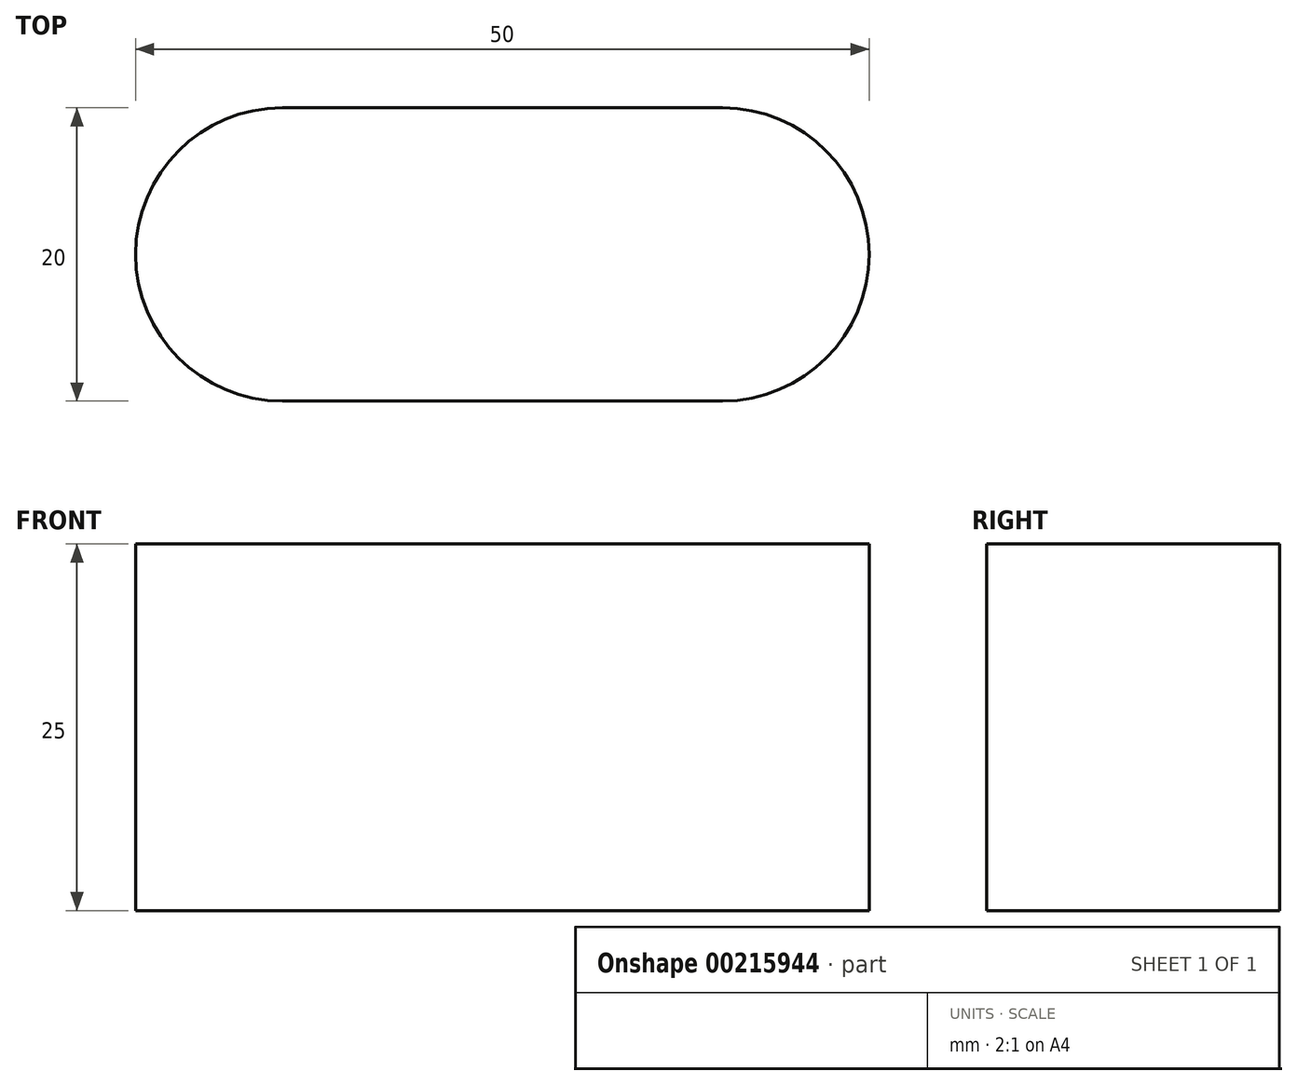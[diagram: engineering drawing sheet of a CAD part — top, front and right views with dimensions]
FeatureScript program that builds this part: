
annotation { "Feature Type Name" : "Feature", "Feature Type Description" : "" }
export const myFeature = defineFeature(function(context is Context, id is Id, definition is map)
    precondition{}
    {
        {
            var Q0;
            Q0=qCreatedBy(makeId("Top.planeOp"),FACE);
            var sketch = newSketch(context, id + "F0", { "sketchPlane" : qUnion([Q0])});
            skLineSegment(sketch, "E0.bottom", {"start": v(15, -10) * mm, "end": v(-15, -10) * mm});
            skLineSegment(sketch, "E0.top", {"start": v(15, 10) * mm, "end": v(-15, 10) * mm});
            skLineSegment(sketch, "E0.left", {"start": v(25, 0) * mm, "end": v(25, 0) * mm});
            skLineSegment(sketch, "E0.right", {"start": v(-25, 0) * mm, "end": v(-25, 0) * mm});
            skPoint(sketch, "E0.middle", {"position": v(0, 0) * mm});
            skPoint(sketch, "E1.visualSharp", {"position": v(-25, 10) * mm});
            skArc(sketch, "E1.filletArc", {"start": v(-15, 10) * mm, "mid": v(-22.07, 7.07) * mm, "end": v(-25, 0) * mm});
            skPoint(sketch, "E2.visualSharp", {"position": v(-25, -10) * mm});
            skArc(sketch, "E2.filletArc", {"start": v(-25, 0) * mm, "mid": v(-22.07, -7.07) * mm, "end": v(-15, -10) * mm});
            skPoint(sketch, "E3.visualSharp", {"position": v(25, -10) * mm});
            skArc(sketch, "E3.filletArc", {"start": v(15, -10) * mm, "mid": v(22.07, -7.07) * mm, "end": v(25, 0) * mm});
            skPoint(sketch, "E4.visualSharp", {"position": v(25, 10) * mm});
            skArc(sketch, "E4.filletArc", {"start": v(25, 0) * mm, "mid": v(22.07, 7.07) * mm, "end": v(15, 10) * mm});
            skSolve(sketch);
        }
        {
            var Q0;
            Q0=makeQuery(id+"F0.imprint","IMPRINT",FACE,{"disambiguationData":[TD([[makeQuery(id+"F0.imprint","IMPRINT",EDGE,{"derivedFrom":sQuery(id+"F0.wireOp",EDGE,"E0.bottom")}),-1.0]])]});
            extrude(context, id + "F1", {"entities" : qUnion([Q0]), "depth" : 25 * mm});
        }
    });
